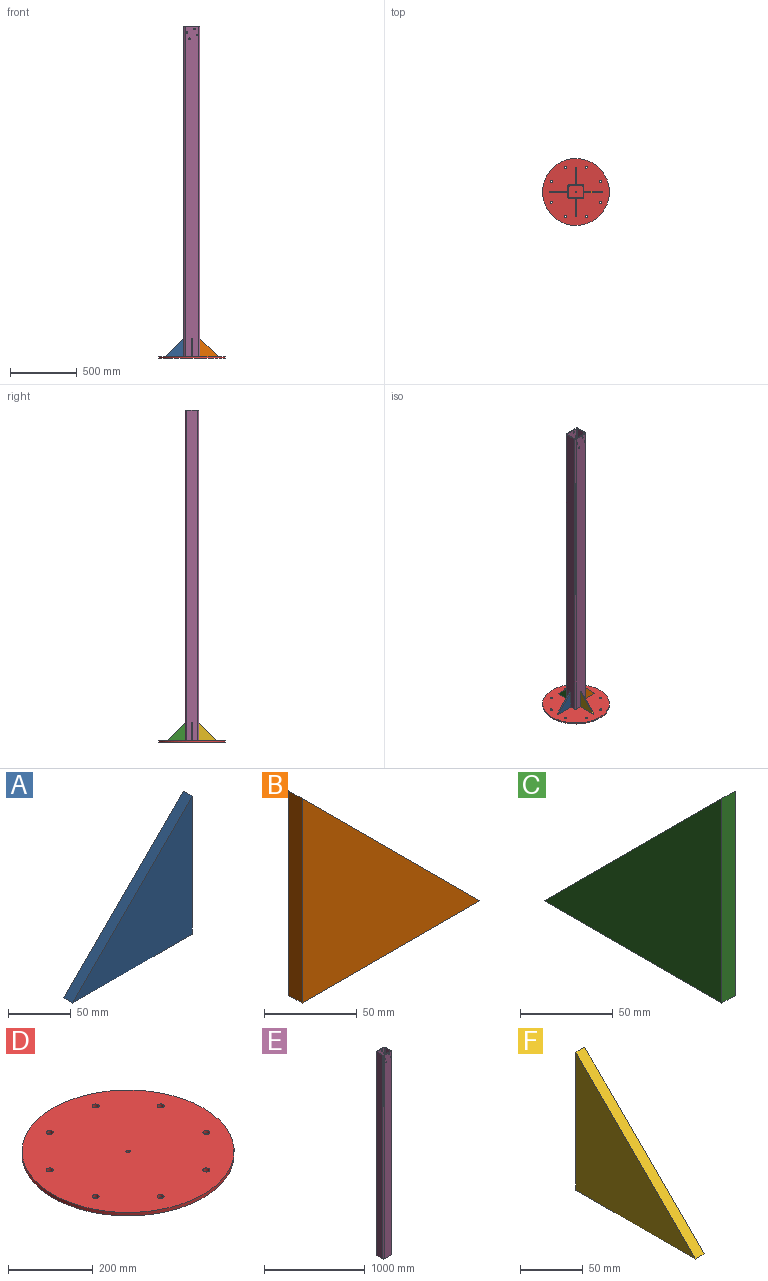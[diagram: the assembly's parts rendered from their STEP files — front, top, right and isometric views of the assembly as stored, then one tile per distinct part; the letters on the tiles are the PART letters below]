
ASSEMBLY  parts=6 mates=1
PART A: 5 faces, bbox 135x10x135 mm
  f0: plane 135x135mm, normal (0,1,0), area 9112.5mm2, adj f2,f3,f4
  f1: plane 135x135mm, normal (0,-1,0), area 9112.5mm2, adj f2,f3,f4
  f2: plane 135x10mm, normal (0,0,-1), area 1350mm2, adj f0,f1,f3,f4
  f3: plane 135x10mm, normal (1,0,0), area 1350mm2, adj f0,f1,f2,f4
  f4: plane 135x135mm, normal (-0.71,0,0.71), area 1909.2mm2, adj f0,f1,f2,f3
PART B: 5 faces, bbox 135x10x135 mm
  f0: plane 135x135mm, normal (0,1,0), area 9112.5mm2, adj f2,f3,f4
  f1: plane 135x135mm, normal (0,-1,0), area 9112.5mm2, adj f2,f3,f4
  f2: plane 135x10mm, normal (0,0,-1), area 1350mm2, adj f0,f1,f3,f4
  f3: plane 135x10mm, normal (-1,0,0), area 1350mm2, adj f0,f1,f2,f4
  f4: plane 135x135mm, normal (0.71,0,0.71), area 1909.2mm2, adj f0,f1,f2,f3
PART C: 5 faces, bbox 10x135x135 mm
  f0: plane 135x135mm, normal (-1,0,0), area 9112.5mm2, adj f2,f3,f4
  f1: plane 135x135mm, normal (1,0,0), area 9112.5mm2, adj f2,f3,f4
  f2: plane 135x135mm, normal (0,0.71,0.71), area 1909.2mm2, adj f0,f1,f3,f4
  f3: plane 135x10mm, normal (0,0,-1), area 1350mm2, adj f0,f1,f2,f4
  f4: plane 135x10mm, normal (0,-1,0), area 1350mm2, adj f0,f1,f2,f3
PART D: 12 faces, bbox 500x500x10 mm
  f0: plane 500x500mm, normal (0,0,-1), area 194560.4mm2, adj f2,f3,f4,f5,f6,f7,f8,f9
  f1: plane 500x500mm, normal (0,0,1), area 194560.4mm2, adj f2,f3,f4,f5,f6,f7,f8,f9
  f2: cylinder r=250mm len=500mm, axis (0,0,1), area 15708mm2, adj f0,f1
  f3: cylinder r=8.25mm len=16.5mm, axis (0,0,1), area 518.4mm2, adj f0,f1
  f4: cylinder r=8.25mm len=16.5mm, axis (0,0,1), area 518.4mm2, adj f0,f1
  f5: cylinder r=8.25mm len=16.5mm, axis (0,0,1), area 518.4mm2, adj f0,f1
  f6: cylinder r=8.25mm len=16.5mm, axis (0,0,1), area 518.4mm2, adj f0,f1
  f7: cylinder r=8.25mm len=16.5mm, axis (0,0,1), area 518.4mm2, adj f0,f1
  f8: cylinder r=8.25mm len=16.5mm, axis (0,0,1), area 518.4mm2, adj f0,f1
  f9: cylinder r=8.25mm len=16.5mm, axis (0,0,1), area 518.4mm2, adj f0,f1
  f10: cylinder r=8.25mm len=16.5mm, axis (0,0,1), area 518.4mm2, adj f0,f1
  f11: cylinder r=5mm len=10mm, axis (0,0,1), area 314.2mm2, adj f0,f1
PART E: 26 faces, bbox 120x100x2475 mm
  f0: plane 2475x80mm, normal (1,0,0), area 198000mm2, adj f1,f2,f13,f25
  f1: cylinder r=5mm len=2475mm, axis (0,0,1), area 19438.6mm2, adj f0,f13,f16,f25
  f2: cylinder r=5mm len=2475mm, axis (0,0,1), area 19438.6mm2, adj f0,f4,f13,f25
  f3: cylinder r=5mm len=2475mm, axis (0,0,1), area 19438.6mm2, adj f4,f13,f14,f25
  f4: plane 2475x100mm, normal (0,1,0), area 247009.1mm2, adj f2,f3,f13,f17,f18,f23,f24,f25
  f5: cylinder r=10mm len=2475mm, axis (0,0,1), area 38877.2mm2, adj f6,f12,f13,f25
  f6: plane 2475x80mm, normal (-1,0,0), area 198000mm2, adj f5,f7,f13,f25
  f7: cylinder r=10mm len=2475mm, axis (0,0,1), area 38877.2mm2, adj f6,f8,f13,f25
  f8: plane 2475x100mm, normal (0,1,0), area 247009.1mm2, adj f7,f9,f13,f19,f20,f21,f22,f25
  f9: cylinder r=10mm len=2475mm, axis (0,0,1), area 38877.2mm2, adj f8,f10,f13,f25
  f10: plane 2475x80mm, normal (1,0,0), area 198000mm2, adj f9,f11,f13,f25
  f11: cylinder r=10mm len=2475mm, axis (0,0,1), area 38877.2mm2, adj f10,f12,f13,f25
  f12: plane 2475x100mm, normal (0,-1,0), area 247009.1mm2, adj f5,f11,f13,f17,f18,f23,f24,f25
  f13: plane 120x100mm, normal (0,0,1), area 2035.6mm2, adj f0,f1,f2,f3,f4,f5,f6,f7
  f14: plane 2475x80mm, normal (-1,0,0), area 198000mm2, adj f3,f13,f15,f25
  f15: cylinder r=5mm len=2475mm, axis (0,0,1), area 19438.6mm2, adj f13,f14,f16,f25
  f16: plane 2475x100mm, normal (0,-1,0), area 247009.1mm2, adj f1,f13,f15,f19,f20,f21,f22,f25
  f17: cylinder r=6.25mm len=12.5mm, axis (0,1,0), area 196.3mm2, adj f4,f12
  f18: cylinder r=6.25mm len=12.5mm, axis (0,1,0), area 196.3mm2, adj f4,f12
  f19: cylinder r=6.25mm len=12.5mm, axis (0,1,0), area 196.3mm2, adj f8,f16
  f20: cylinder r=6.25mm len=12.5mm, axis (0,1,0), area 196.3mm2, adj f8,f16
  f21: cylinder r=6.25mm len=12.5mm, axis (0,1,0), area 196.3mm2, adj f8,f16
  f22: cylinder r=6.25mm len=12.5mm, axis (0,1,0), area 196.3mm2, adj f8,f16
  f23: cylinder r=6.25mm len=12.5mm, axis (0,1,0), area 196.3mm2, adj f4,f12
  f24: cylinder r=6.25mm len=12.5mm, axis (0,1,0), area 196.3mm2, adj f4,f12
  f25: plane 120x100mm, normal (0,0,-1), area 2035.6mm2, adj f0,f1,f2,f3,f4,f5,f6,f7
PART F: 5 faces, bbox 10x135x135 mm
  f0: plane 135x135mm, normal (-1,0,0), area 9112.5mm2, adj f2,f3,f4
  f1: plane 135x135mm, normal (1,0,0), area 9112.5mm2, adj f2,f3,f4
  f2: plane 135x135mm, normal (0,-0.71,0.71), area 1909.2mm2, adj f0,f1,f3,f4
  f3: plane 135x10mm, normal (0,0,-1), area 1350mm2, adj f0,f1,f2,f4
  f4: plane 135x10mm, normal (0,1,0), area 1350mm2, adj f0,f1,f2,f3
PLACE A at identity
PLACE B at identity
PLACE C at identity
PLACE D at identity
PLACE E t=(0,0,75)mm
PLACE F at identity
MATE planar E.f25 <-> D.f2  axis (0,0,-1) through (0,0,10)mm
